# Revit family: Atlas BTW Top entry pan
name_source: partatom
category: Plumbing Fixtures
units: mm (PartAtom-declared; Revit-internal decimal feet)

## family parameters
Always vertical = Yes
Cut with Voids When Loaded = No
Enable Cutting in Views = No
Maintain Annotation Orientation = No
OmniClass Number = 23.45.05.21.11.11
OmniClass Title = Water Operated Water Closets
Part Type = Normal
Room Calculation Point = No
Round Connector Dimension = Use Diameter
Shared = No
Work Plane-Based = No

## types (1)
- Atlas BTW Top entry pan
    Category = Back To Wall Pans
    Colour = White
    Default Elevation = 0 mm  [stored 0 ft]
    Manufacturer = Lecico South Africa
    Material = Vitreous China
    Model = Atlas BTW Top entry pan
    Product Code = ATLPANBTW0TOPUE
    Technical Dimensions = W366 x H395 x D566mm
    URL = https://www.lecicosa.co.za

note: [stored X ft] marks values corroborated as IEEE doubles in the binary element streams (Revit-internal decimal feet)

## geometry (parser evidence)
native form markers: Sweep x3
no freeform markers — native parametric forms only
